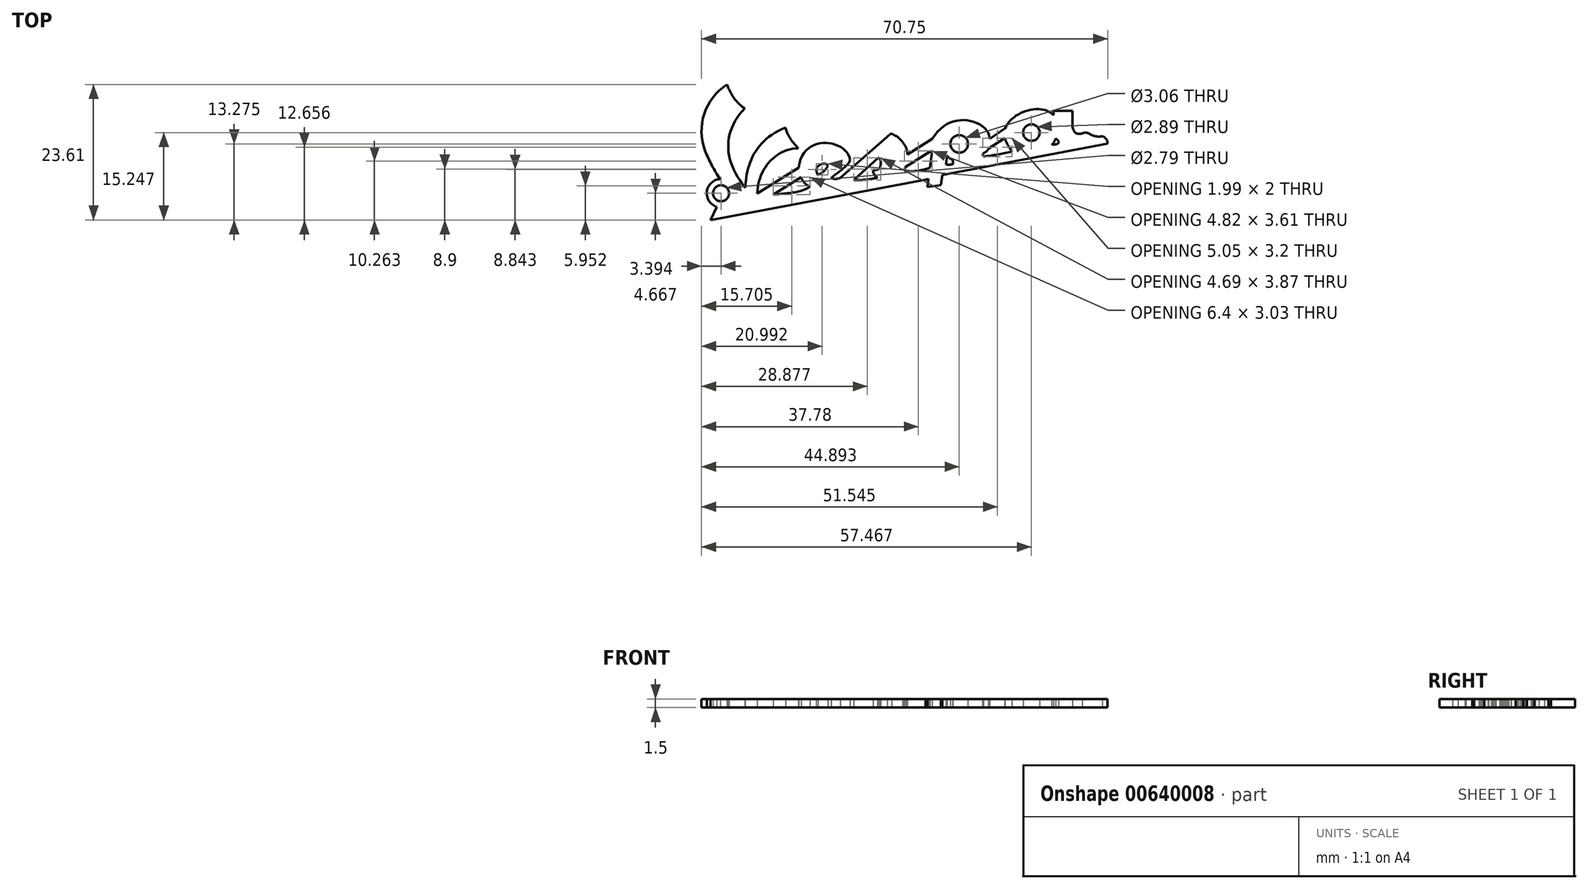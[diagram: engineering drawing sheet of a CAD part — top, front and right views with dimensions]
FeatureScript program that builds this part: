
annotation { "Feature Type Name" : "Feature", "Feature Type Description" : "" }
export const myFeature = defineFeature(function(context is Context, id is Id, definition is map)
    precondition{}
    {
        {
            var Q0;
            Q0=qCreatedBy(makeId("Top.planeOp"),FACE);
            var sketch = newSketch(context, id + "F0", { "sketchPlane" : qUnion([Q0])});
            skLineSegment(sketch, "E0", {"start": v(-27.86, -14.21) * mm, "end": v(-28.97, -16.5) * mm});
            skLineSegment(sketch, "E1", {"start": v(-28.97, -16.5) * mm, "end": v(8.49, -9.47) * mm});
            skLineSegment(sketch, "E2", {"start": v(11.42, -8.66) * mm, "end": v(39.49, -3.33) * mm});
            skLineSegment(sketch, "E3", {"start": v(39.49, -3.33) * mm, "end": v(40.22, -3.19) * mm});
            skLineSegment(sketch, "E4", {"start": v(8.81, -10.76) * mm, "end": v(9, -9.32) * mm});
            skLineSegment(sketch, "E5", {"start": v(9, -9.32) * mm, "end": v(8.49, -9.47) * mm});
            skLineSegment(sketch, "E6", {"start": v(8.81, -10.76) * mm, "end": v(11.17, -10.44) * mm});
            skLineSegment(sketch, "E7", {"start": v(11.17, -10.44) * mm, "end": v(11.42, -8.66) * mm});
            skSolve(sketch);
        }
        {
            var Q0;
            Q0=qCreatedBy(makeId("Top.planeOp"),FACE);
            var sketch = newSketch(context, id + "F1", { "sketchPlane" : qUnion([Q0])});
            skArc(sketch, "E8", {"start": v(-26.1, 7.11) * mm, "mid": v(-30.06, 2.02) * mm, "end": v(-29.9, -4.43) * mm});
            skArc(sketch, "E9", {"start": v(-29.9, -4.43) * mm, "mid": v(-28.74, -6.97) * mm, "end": v(-27.28, -9.35) * mm});
            skFitSpline(sketch, "E10", {"points": [v(-22.93, -10.83) * mm, v(-15.9, -0.36) * mm], "startDerivative": vector(0.83, 13.4) * mm, "endDerivative": vector(15.53, 6.52) * mm});
            skFitSpline(sketch, "E11", {"points": [v(-26.1, 7.11) * mm, v(-23.02, 2.96) * mm], "startDerivative": vector(2.09, -5.04) * mm, "endDerivative": vector(4.74, -3.08) * mm});
            skPoint(sketch, "E12.1.internal.snap0", {"position": v(-27.28, -9.35) * mm});
            skFitSpline(sketch, "E13", {"points": [v(-23.02, 2.96) * mm, v(-22.93, -10.83) * mm], "startDerivative": vector(-11.68, -12.28) * mm, "endDerivative": vector(11.62, -14) * mm});
            skFitSpline(sketch, "E14", {"points": [v(-15.9, -0.36) * mm, v(-13.67, -3.98) * mm], "startDerivative": vector(0.64, -4.16) * mm, "endDerivative": vector(2.51, -2.51) * mm});
            skFitSpline(sketch, "E15", {"points": [v(-13.67, -3.98) * mm, v(-20.82, -11.86) * mm], "startDerivative": vector(-12.07, -0.34) * mm, "endDerivative": vector(-0.34, -12.74) * mm});
            skLineSegment(sketch, "E16", {"start": v(-20.82, -11.86) * mm, "end": v(-13.6, -7.35) * mm});
            skLineSegment(sketch, "E17", {"start": v(-18.02, -12.06) * mm, "end": v(-13.18, -9.04) * mm});
            skFitSpline(sketch, "E18", {"points": [v(-13.18, -9.04) * mm, v(-11.63, -10.66) * mm], "startDerivative": vector(0.51, -1.6) * mm, "endDerivative": vector(2.7, -0.92) * mm});
            skFitSpline(sketch, "E19", {"points": [v(-18.02, -12.06) * mm, v(-11.63, -10.66) * mm], "startDerivative": vector(6.94, 0.68) * mm, "endDerivative": vector(4.37, 3.27) * mm});
            skFitSpline(sketch, "E20", {"points": [v(-13.6, -7.35) * mm, v(-4.67, -5.95) * mm], "startDerivative": vector(1.96, 18.25) * mm, "endDerivative": vector(1.48, -10.5) * mm});
            skFitSpline(sketch, "E21", {"points": [v(-4.67, -5.95) * mm, v(-7.93, -9.17) * mm], "startDerivative": vector(-0.12, -2.79) * mm, "endDerivative": vector(-3.62, -3.14) * mm});
            skFitSpline(sketch, "E22", {"points": [v(-10.24, -8.66) * mm, v(-8.54, -7.11) * mm], "startDerivative": vector(1.84, 0.71) * mm, "endDerivative": vector(0.95, 1.96) * mm});
            skFitSpline(sketch, "E23", {"points": [v(-10.24, -8.66) * mm, v(-10.24, -7.1) * mm], "startDerivative": vector(-1.36, 2.2) * mm, "endDerivative": vector(0.94, 0.73) * mm});
            skFitSpline(sketch, "E24", {"points": [v(-10.24, -7.1) * mm, v(-8.54, -7.11) * mm], "startDerivative": vector(2.22, 1.73) * mm, "endDerivative": vector(0.47, -1.84) * mm});
            skFitSpline(sketch, "E25", {"points": [v(-7.93, -9.17) * mm, v(-6.35, -9.17) * mm], "startDerivative": vector(1.19, -0.83) * mm, "endDerivative": vector(1.3, 0.41) * mm});
            skLineSegment(sketch, "E26", {"start": v(-6.35, -9.17) * mm, "end": v(1.83, -1.96) * mm});
            skFitSpline(sketch, "E27", {"points": [v(1.83, -1.96) * mm, v(2.61, -1.48) * mm], "startDerivative": vector(0.9, 0.72) * mm, "endDerivative": vector(0.71, -0.24) * mm});
            skFitSpline(sketch, "E28", {"points": [v(2.61, -1.48) * mm, v(4.5, -2.9) * mm], "startDerivative": vector(2.24, -0.95) * mm, "endDerivative": vector(1.2, -1.74) * mm});
            skLineSegment(sketch, "E29", {"start": v(-4, -9.53) * mm, "end": v(0.27, -5.67) * mm});
            skFitSpline(sketch, "E30", {"points": [v(0.27, -5.67) * mm, v(0.57, -7.24) * mm], "startDerivative": vector(1.62, -0.02) * mm, "endDerivative": vector(-0.52, -1.24) * mm});
            skFitSpline(sketch, "E31", {"points": [v(-0.66, -7.9) * mm, v(0.57, -7.24) * mm], "startDerivative": vector(1.16, 0.68) * mm, "endDerivative": vector(-0.07, 1.8) * mm});
            skFitSpline(sketch, "E32", {"points": [v(-4, -9.53) * mm, v(0.12, -9.12) * mm], "startDerivative": vector(4.04, -0.05) * mm, "endDerivative": vector(3.69, 0.95) * mm});
            skFitSpline(sketch, "E33", {"points": [v(0.12, -9.12) * mm, v(-0.66, -7.9) * mm], "startDerivative": vector(-1.8, 1.2) * mm, "endDerivative": vector(-0.2, 1.2) * mm});
            skFitSpline(sketch, "E34", {"points": [v(4.5, -2.9) * mm, v(5.3, -5.08) * mm], "startDerivative": vector(1.73, -2.25) * mm, "endDerivative": vector(-0.05, -2.44) * mm});
            skLineSegment(sketch, "E35", {"start": v(5.3, -5.08) * mm, "end": v(9.66, -2.38) * mm});
            skLineSegment(sketch, "E36", {"start": v(4.99, -7.25) * mm, "end": v(9.26, -4.6) * mm});
            skFitSpline(sketch, "E37", {"points": [v(4.99, -7.25) * mm, v(4.99, -8.04) * mm], "startDerivative": vector(-0.6, -0.95) * mm, "endDerivative": vector(0.6, -0.53) * mm});
            skFitSpline(sketch, "E38", {"points": [v(4.99, -8.04) * mm, v(9.06, -7.45) * mm], "startDerivative": vector(4.09, 0) * mm, "endDerivative": vector(3.14, 1.3) * mm});
            skLineSegment(sketch, "E39", {"start": v(9.28, -7.38) * mm, "end": v(9.66, -4.43) * mm});
            skFitSpline(sketch, "E40", {"points": [v(9.06, -7.45) * mm, v(9.28, -7.38) * mm], "startDerivative": vector(0.23, 0.06) * mm, "endDerivative": vector(0.23, 0.06) * mm});
            skFitSpline(sketch, "E41", {"points": [v(9.26, -4.6) * mm, v(9.66, -4.43) * mm], "startDerivative": vector(0.4, 0.17) * mm, "endDerivative": vector(0.4, 0.17) * mm});
            skFitSpline(sketch, "E42", {"points": [v(9.66, -2.38) * mm, v(19.64, -2.38) * mm], "startDerivative": vector(10.18, 17.25) * mm, "endDerivative": vector(-0.67, -8.53) * mm});
            skCircle(sketch, "E43", {"center": v(14.36, -3.23) * mm, "radius": 1.53 * mm});
            skLineSegment(sketch, "E44", {"start": v(12.05, -6.81) * mm, "end": v(12.25, -5.26) * mm});
            skFitSpline(sketch, "E45", {"points": [v(12.25, -5.26) * mm, v(13.23, -6) * mm], "startDerivative": vector(0.55, -0.86) * mm, "endDerivative": vector(1.32, -0.45) * mm});
            skFitSpline(sketch, "E46", {"points": [v(13.23, -6) * mm, v(13.23, -6.8) * mm], "startDerivative": vector(0.14, -0.69) * mm, "endDerivative": vector(-0.1, -0.83) * mm});
            skFitSpline(sketch, "E47", {"points": [v(12.05, -6.81) * mm, v(13.23, -6.8) * mm], "startDerivative": vector(1.04, -0.11) * mm, "endDerivative": vector(1.18, 0.12) * mm});
            skLineSegment(sketch, "E48", {"start": v(19.64, -2.38) * mm, "end": v(22.37, -0.53) * mm});
            skLineSegment(sketch, "E49", {"start": v(19.43, -4.06) * mm, "end": v(22.31, -2.24) * mm});
            skFitSpline(sketch, "E50", {"points": [v(19.43, -4.06) * mm, v(18.6, -4.82) * mm], "startDerivative": vector(-0.25, -1.34) * mm, "endDerivative": vector(-0.67, -0.3) * mm});
            skFitSpline(sketch, "E51", {"points": [v(18.6, -4.82) * mm, v(18.6, -5.44) * mm], "startDerivative": vector(-0.46, -0.63) * mm, "endDerivative": vector(0.38, -0.63) * mm});
            skFitSpline(sketch, "E52", {"points": [v(18.6, -5.44) * mm, v(23.54, -4.58) * mm], "startDerivative": vector(4.78, 0.63) * mm, "endDerivative": vector(4.73, 1.05) * mm});
            skFitSpline(sketch, "E53", {"points": [v(23.54, -4.58) * mm, v(22.31, -2.24) * mm], "startDerivative": vector(-1.59, 2.3) * mm, "endDerivative": vector(-0.72, 2.18) * mm});
            skFitSpline(sketch, "E54", {"points": [v(22.37, -0.53) * mm, v(30.8, 1.77) * mm], "startDerivative": vector(3.2, 8.48) * mm, "endDerivative": vector(6.68, -7.03) * mm});
            skCircle(sketch, "E55", {"center": v(26.94, -1.25) * mm, "radius": 1.44 * mm});
            skLineSegment(sketch, "E56", {"start": v(30.8, 1.77) * mm, "end": v(30.8, 2.52) * mm});
            skLineSegment(sketch, "E57", {"start": v(30.8, 2.52) * mm, "end": v(34.07, 2.52) * mm});
            skLineSegment(sketch, "E58", {"start": v(34.07, 2.52) * mm, "end": v(34.07, 0) * mm});
            skFitSpline(sketch, "E59", {"points": [v(34.07, 0) * mm, v(35.83, -1.37) * mm], "startDerivative": vector(0.2, -3.16) * mm, "endDerivative": vector(3.44, 1.2) * mm});
            skFitSpline(sketch, "E60", {"points": [v(35.83, -1.37) * mm, v(39.3, -1.9) * mm], "startDerivative": vector(3.5, 1.66) * mm, "endDerivative": vector(6.28, 0.98) * mm});
            skFitSpline(sketch, "E61", {"points": [v(39.3, -1.9) * mm, v(39.92, -2.3) * mm, v(40.07, -2.52) * mm, v(40.22, -3.19) * mm], "startDerivative": vector(2.35, -0.6) * mm, "endDerivative": vector(-0.16, -2.67) * mm});
            skFitSpline(sketch, "E62", {"points": [v(31.14, -2.37) * mm, v(30.48, -3.31) * mm], "startDerivative": vector(-0.4, -0.95) * mm, "endDerivative": vector(-0.9, -0.6) * mm});
            skFitSpline(sketch, "E63", {"points": [v(31.14, -2.37) * mm, v(31.68, -3.08) * mm], "startDerivative": vector(1.05, -0.05) * mm, "endDerivative": vector(0.05, -1.25) * mm});
            skFitSpline(sketch, "E64", {"points": [v(31.68, -3.08) * mm, v(30.48, -3.31) * mm], "startDerivative": vector(-1.35, -1) * mm, "endDerivative": vector(-1, 0.1) * mm});
            skArc(sketch, "E65", {"start": v(-27.28, -9.35) * mm, "mid": v(-29.6, -11.54) * mm, "end": v(-27.86, -14.21) * mm});
            skCircle(sketch, "E66", {"center": v(-27.14, -11.83) * mm, "radius": 1.4 * mm});
            skLineSegment(sketch, "E67.0", {"start": v(-27.86, -14.21) * mm, "end": v(-28.97, -16.5) * mm});
            skLineSegment(sketch, "E68.0", {"start": v(-28.97, -16.5) * mm, "end": v(8.49, -9.47) * mm});
            skPoint(sketch, "E69.0", {"position": v(8.9, -10.04) * mm});
            skLineSegment(sketch, "E70.0", {"start": v(8.81, -10.76) * mm, "end": v(11.17, -10.44) * mm});
            skLineSegment(sketch, "E71.0", {"start": v(8.81, -10.76) * mm, "end": v(9, -9.32) * mm});
            skPoint(sketch, "E72.0", {"position": v(8.75, -9.4) * mm});
            skLineSegment(sketch, "E73.0", {"start": v(9, -9.32) * mm, "end": v(8.49, -9.47) * mm});
            skLineSegment(sketch, "E74.0", {"start": v(11.42, -8.66) * mm, "end": v(39.49, -3.33) * mm});
            skLineSegment(sketch, "E75.0", {"start": v(11.17, -10.44) * mm, "end": v(11.42, -8.66) * mm});
            skLineSegment(sketch, "E76.0", {"start": v(39.49, -3.33) * mm, "end": v(40.22, -3.19) * mm});
            skSolve(sketch);
        }
        {
            var Q0;
            Q0=makeQuery(id+"F1.imprint","IMPRINT",FACE,{"disambiguationData":[TD([[makeQuery(id+"F1.imprint","IMPRINT",EDGE,{"derivedFrom":sQuery(id+"F1.wireOp",EDGE,"E8")}),1.0]])]});
            extrude(context, id + "F2", {"entities" : qUnion([Q0]), "depth" : 1.5 * mm, "offsetDistance" : 25 * mm});
        }
    });
